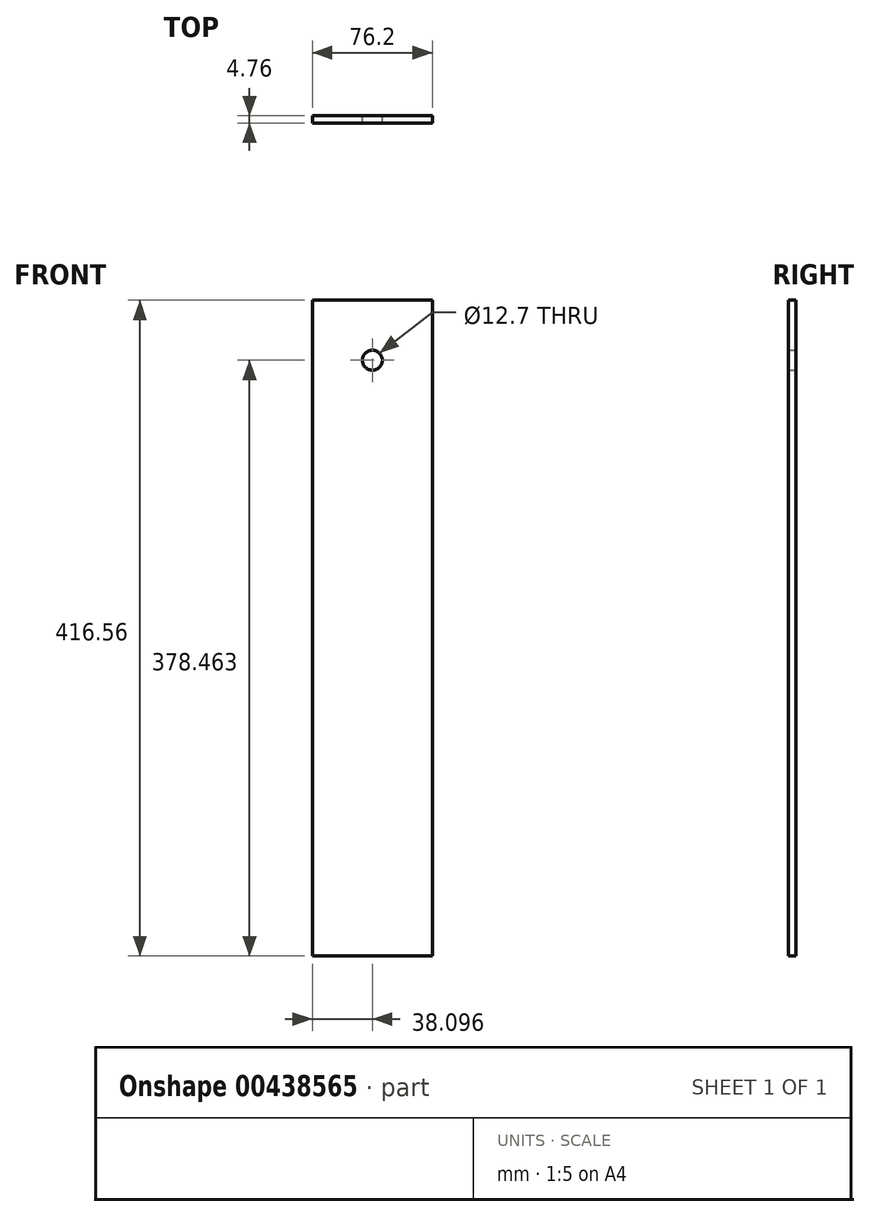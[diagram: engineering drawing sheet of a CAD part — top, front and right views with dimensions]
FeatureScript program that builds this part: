
annotation { "Feature Type Name" : "Feature", "Feature Type Description" : "" }
export const myFeature = defineFeature(function(context is Context, id is Id, definition is map)
    precondition{}
    {
        {
            var Q0;
            Q0=qCreatedBy(makeId("Front.planeOp"),FACE);
            var sketch = newSketch(context, id + "F0", { "sketchPlane" : qUnion([Q0])});
            skLineSegment(sketch, "E0.bottom", {"start": v(-47.77, 359.71) * mm, "end": v(28.43, 359.71) * mm});
            skLineSegment(sketch, "E0.top", {"start": v(-47.77, -56.85) * mm, "end": v(28.43, -56.85) * mm});
            skLineSegment(sketch, "E0.left", {"start": v(-47.77, 359.71) * mm, "end": v(-47.77, -56.85) * mm});
            skLineSegment(sketch, "E0.right", {"start": v(28.43, 359.71) * mm, "end": v(28.43, -56.85) * mm});
            skPoint(sketch, "E1", {"position": v(-9.67, 359.71) * mm});
            skPoint(sketch, "E2", {"position": v(-9.67, 321.61) * mm});
            skCircle(sketch, "E3", {"center": v(-9.67, 321.61) * mm, "radius": 6.35 * mm});
            skSolve(sketch);
        }
        {
            var Q0;
            Q0=makeQuery(id+"F0.imprint","IMPRINT",FACE,{"disambiguationData":[TD([[makeQuery(id+"F0.imprint","IMPRINT",EDGE,{"derivedFrom":sQuery(id+"F0.wireOp",EDGE,"E0.bottom")}),-1.0]])]});
            extrude(context, id + "F1", {"entities" : qUnion([Q0]), "depth" : 4.76 * mm});
        }
    });
